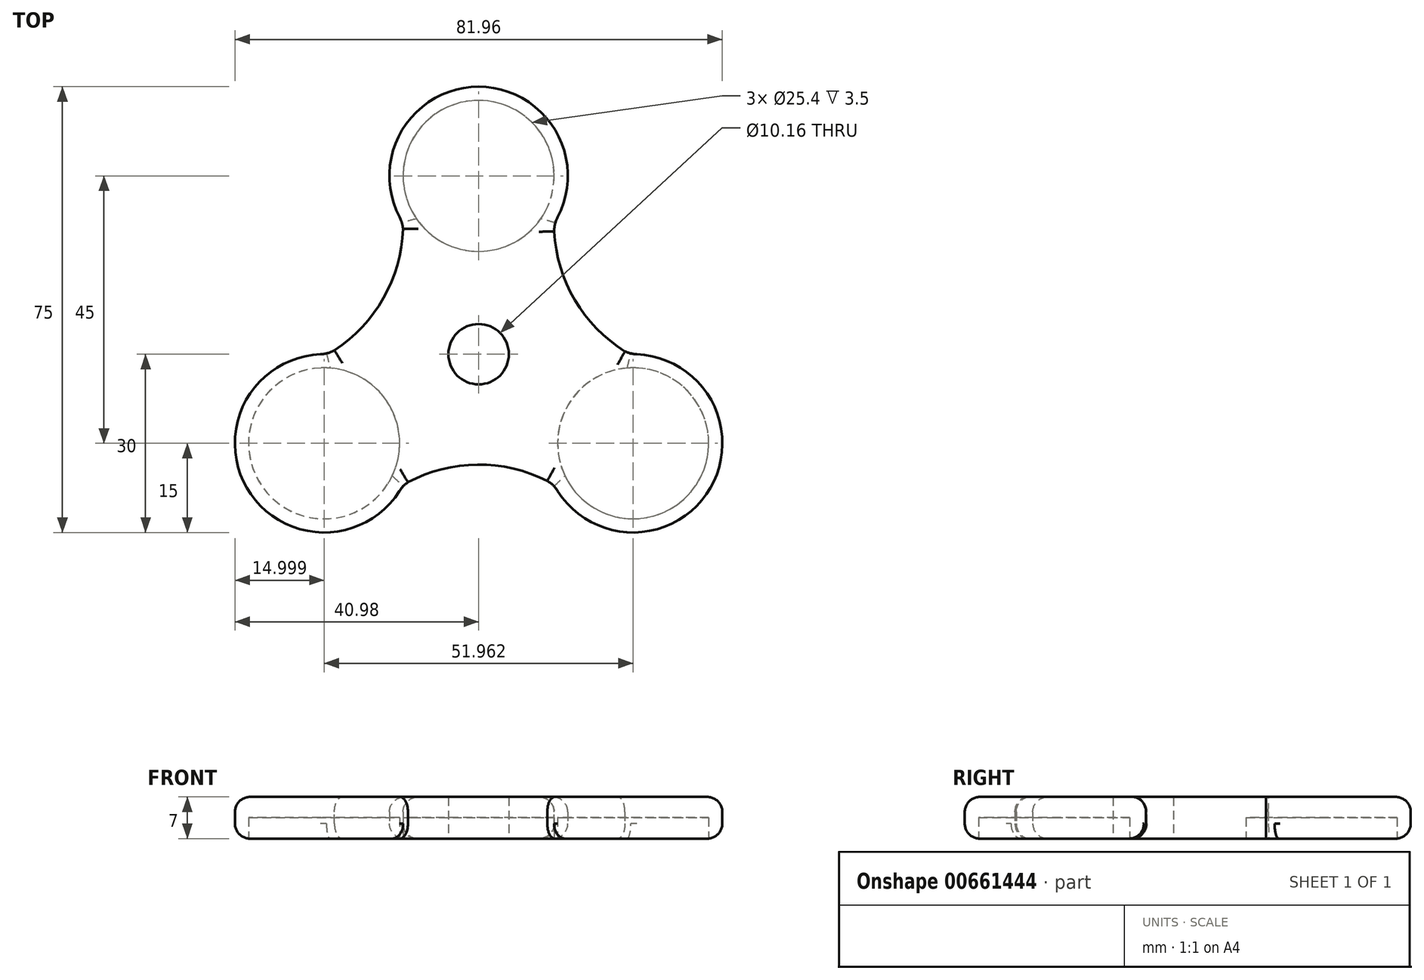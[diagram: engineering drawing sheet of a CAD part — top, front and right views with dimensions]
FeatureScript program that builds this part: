
annotation { "Feature Type Name" : "Feature", "Feature Type Description" : "" }
export const myFeature = defineFeature(function(context is Context, id is Id, definition is map)
    precondition{}
    {
        {
            var Q0;
            Q0=qCreatedBy(makeId("Top.planeOp"),FACE);
            var sketch = newSketch(context, id + "F0", { "sketchPlane" : qUnion([Q0])});
            skCircle(sketch, "E0", {"center": v(0, 0) * mm, "radius": 15 * mm});
            skCircle(sketch, "E1", {"center": v(0, 30) * mm, "radius": 15 * mm});
            skCircle(sketch, "E2", {"center": v(0, 30) * mm, "radius": 12.7 * mm});
            skCircle(sketch, "E3", {"center": v(0, 0) * mm, "radius": 5.08 * mm});
            skLineSegment(sketch, "E4", {"start": v(0, 30) * mm, "end": v(0, 15) * mm, "construction": true});
            skLineSegment(sketch, "E5", {"start": v(0, 0) * mm, "end": v(0, 15) * mm, "construction": true});
            skLineSegment(sketch, "E6", {"start": v(0, 0) * mm, "end": v(0, -15) * mm});
            skLineSegment(sketch, "E7", {"start": v(0, 0) * mm, "end": v(15, 0) * mm});
            skLineSegment(sketch, "E8", {"start": v(0, 0) * mm, "end": v(-15, 0) * mm});
            skLineSegment(sketch, "E9", {"start": v(0, 30) * mm, "end": v(-20.54, 30) * mm, "construction": true});
            skLineSegment(sketch, "E10", {"start": v(-25.98, -15) * mm, "end": v(-25.98, 30.15) * mm, "construction": true});
            skPoint(sketch, "E11", {"position": v(-25.98, 0) * mm});
            skPoint(sketch, "E12", {"position": v(-15, 30) * mm});
            skLineSegment(sketch, "E13.0", {"start": v(12.7, 30) * mm, "end": v(12.7, 15) * mm});
            skLineSegment(sketch, "E13.1", {"start": v(12.7, 0) * mm, "end": v(12.7, 15) * mm});
            skLineSegment(sketch, "E14.0", {"start": v(-12.7, 30) * mm, "end": v(-12.7, 15) * mm});
            skLineSegment(sketch, "E14.1", {"start": v(-12.7, 0) * mm, "end": v(-12.7, 15) * mm});
            skPoint(sketch, "E15.1.0", {"position": v(-18.48, -28) * mm});
            skLineSegment(sketch, "E15.1.1", {"start": v(-19.63, -26) * mm, "end": v(-6.64, -18.5) * mm});
            skLineSegment(sketch, "E15.1.2", {"start": v(-32.33, -4) * mm, "end": v(-19.34, 3.5) * mm});
            skLineSegment(sketch, "E15.1.3", {"start": v(-25.98, -15) * mm, "end": v(-15.71, -32.78) * mm, "construction": true});
            skLineSegment(sketch, "E15.1.4", {"start": v(-25.98, -15) * mm, "end": v(-13, -7.5) * mm, "construction": true});
            skCircle(sketch, "E15.1.5", {"center": v(-25.98, -15) * mm, "radius": 12.7 * mm});
            skCircle(sketch, "E15.1.6", {"center": v(-25.98, -15) * mm, "radius": 15 * mm});
            skLineSegment(sketch, "E15.1.7", {"start": v(6.35, -11) * mm, "end": v(-6.64, -18.5) * mm});
            skLineSegment(sketch, "E15.1.8", {"start": v(-6.35, 11) * mm, "end": v(-19.34, 3.5) * mm});
            skLineSegment(sketch, "E15.1.9", {"start": v(0, 0) * mm, "end": v(-13, -7.5) * mm, "construction": true});
            skPoint(sketch, "E15.2.0", {"position": v(33.48, -2) * mm});
            skLineSegment(sketch, "E15.2.1", {"start": v(32.33, -4) * mm, "end": v(19.34, 3.5) * mm});
            skLineSegment(sketch, "E15.2.2", {"start": v(19.63, -26) * mm, "end": v(6.64, -18.5) * mm});
            skLineSegment(sketch, "E15.2.3", {"start": v(25.98, -15) * mm, "end": v(36.25, 2.78) * mm, "construction": true});
            skLineSegment(sketch, "E15.2.4", {"start": v(25.98, -15) * mm, "end": v(13, -7.5) * mm, "construction": true});
            skCircle(sketch, "E15.2.5", {"center": v(25.98, -15) * mm, "radius": 12.7 * mm});
            skCircle(sketch, "E15.2.6", {"center": v(25.98, -15) * mm, "radius": 15 * mm});
            skLineSegment(sketch, "E15.2.7", {"start": v(6.35, 11) * mm, "end": v(19.34, 3.5) * mm});
            skLineSegment(sketch, "E15.2.8", {"start": v(-6.35, -11) * mm, "end": v(6.64, -18.5) * mm});
            skLineSegment(sketch, "E15.2.9", {"start": v(0, 0) * mm, "end": v(13, -7.5) * mm, "construction": true});
            skSolve(sketch);
        }
        {
            var Q0;
            {var subQ0=sQuery(id+"F0.wireOp",EDGE,"E14.0");var subQ1=sQuery(id+"F0.wireOp",EDGE,"E1");var subQ2=makeQuery(id+"F0.imprint","INTERSECT",VERTEX,{"derivedFrom":[subQ1,subQ0]});Q0=makeQuery(id+"F0.imprint","IMPRINT",FACE,{"disambiguationData":[TD([[makeQuery(id+"F0.imprint","IMPRINT",EDGE,{"disambiguationData":[TD([[subQ2,1.0]])],"derivedFrom":subQ1}),1.0]])]});}
            var Q1;
            {var subQ0=sQuery(id+"F0.wireOp",EDGE,"E13.1");var subQ1=sQuery(id+"F0.wireOp",EDGE,"E0");var subQ2=makeQuery(id+"F0.imprint","INTERSECT",VERTEX,{"derivedFrom":[subQ1,subQ0]});Q1=makeQuery(id+"F0.imprint","IMPRINT",FACE,{"disambiguationData":[TD([[makeQuery(id+"F0.imprint","IMPRINT",EDGE,{"disambiguationData":[TD([[subQ2,-1.0]])],"derivedFrom":subQ1}),-1.0]])]});}
            var Q2;
            {var subQ0=sQuery(id+"F0.wireOp",EDGE,"E14.1");var subQ1=sQuery(id+"F0.wireOp",EDGE,"E0");var subQ2=makeQuery(id+"F0.imprint","INTERSECT",VERTEX,{"derivedFrom":[subQ1,subQ0]});Q2=makeQuery(id+"F0.imprint","IMPRINT",FACE,{"disambiguationData":[TD([[makeQuery(id+"F0.imprint","IMPRINT",EDGE,{"disambiguationData":[TD([[subQ2,1.0]])],"derivedFrom":subQ1}),-1.0]])]});}
            var Q3;
            {var subQ1=sQuery(id+"F0.wireOp",EDGE,"E1");var subQ5=sQuery(id+"F0.wireOp",EDGE,"E14.0");var subQ8=makeQuery(id+"F0.imprint","INTERSECT",VERTEX,{"derivedFrom":[subQ1,subQ5]});Q3=makeQuery(id+"F0.imprint","IMPRINT",FACE,{"disambiguationData":[TD([[makeQuery(id+"F0.imprint","IMPRINT",EDGE,{"disambiguationData":[TD([[subQ8,-1.0]])],"derivedFrom":subQ1}),1.0]])]});}
            var Q4;
            {var subQ0=sQuery(id+"F0.wireOp",EDGE,"E13.1");var subQ5=sQuery(id+"F0.wireOp",EDGE,"E0");var subQ6=makeQuery(id+"F0.imprint","INTERSECT",VERTEX,{"derivedFrom":[subQ5,subQ0]});Q4=makeQuery(id+"F0.imprint","IMPRINT",FACE,{"disambiguationData":[TD([[makeQuery(id+"F0.imprint","IMPRINT",EDGE,{"disambiguationData":[TD([[subQ6,-1.0]])],"derivedFrom":subQ5}),1.0]])]});}
            var Q5;
            {var subQ0=sQuery(id+"F0.wireOp",EDGE,"E7");var subQ1=sQuery(id+"F0.wireOp",EDGE,"E0");var subQ2=makeQuery(id+"F0.imprint","INTERSECT",VERTEX,{"derivedFrom":[subQ1,subQ0]});Q5=makeQuery(id+"F0.imprint","IMPRINT",FACE,{"disambiguationData":[TD([[makeQuery(id+"F0.imprint","IMPRINT",EDGE,{"disambiguationData":[TD([[subQ2,-1.0]])],"derivedFrom":subQ1}),1.0]])]});}
            var Q6;
            {var subQ3=sQuery(id+"F0.wireOp",EDGE,"E0");var subQ7=makeQuery(id+"F0.imprint","INTERSECT",VERTEX,{"derivedFrom":[subQ3,sQuery(id+"F0.wireOp",EDGE,"E7")]});Q6=makeQuery(id+"F0.imprint","IMPRINT",FACE,{"disambiguationData":[TD([[makeQuery(id+"F0.imprint","IMPRINT",EDGE,{"disambiguationData":[TD([[subQ7,-1.0]])],"derivedFrom":subQ3}),-1.0]])]});}
            var Q7;
            {var subQ0=sQuery(id+"F0.wireOp",EDGE,"E15.2.6");var subQ1=sQuery(id+"F0.wireOp",EDGE,"E15.2.1");var subQ2=makeQuery(id+"F0.imprint","INTERSECT",VERTEX,{"derivedFrom":[subQ1,subQ0]});Q7=makeQuery(id+"F0.imprint","IMPRINT",FACE,{"disambiguationData":[TD([[makeQuery(id+"F0.imprint","IMPRINT",EDGE,{"disambiguationData":[TD([[subQ2,1.0]])],"derivedFrom":subQ1}),1.0]])]});}
            var Q8;
            {var subQ0=sQuery(id+"F0.wireOp",EDGE,"E15.2.6");var subQ1=sQuery(id+"F0.wireOp",EDGE,"E15.2.1");var subQ2=makeQuery(id+"F0.imprint","INTERSECT",VERTEX,{"derivedFrom":[subQ1,subQ0]});Q8=makeQuery(id+"F0.imprint","IMPRINT",FACE,{"disambiguationData":[TD([[makeQuery(id+"F0.imprint","IMPRINT",EDGE,{"disambiguationData":[TD([[subQ2,1.0]])],"derivedFrom":subQ1}),-1.0]])]});}
            var Q9;
            {var subQ0=sQuery(id+"F0.wireOp",EDGE,"E15.2.8");var subQ1=sQuery(id+"F0.wireOp",EDGE,"E0");var subQ2=makeQuery(id+"F0.imprint","INTERSECT",VERTEX,{"derivedFrom":[subQ1,subQ0]});Q9=makeQuery(id+"F0.imprint","IMPRINT",FACE,{"disambiguationData":[TD([[makeQuery(id+"F0.imprint","IMPRINT",EDGE,{"disambiguationData":[TD([[subQ2,-1.0]])],"derivedFrom":subQ1}),-1.0]])]});}
            var Q10;
            {var subQ5=sQuery(id+"F0.wireOp",EDGE,"E15.2.8");var subQ6=sQuery(id+"F0.wireOp",EDGE,"E0");var subQ7=makeQuery(id+"F0.imprint","INTERSECT",VERTEX,{"derivedFrom":[subQ6,subQ5]});Q10=makeQuery(id+"F0.imprint","IMPRINT",FACE,{"disambiguationData":[TD([[makeQuery(id+"F0.imprint","IMPRINT",EDGE,{"disambiguationData":[TD([[subQ7,-1.0]])],"derivedFrom":subQ6}),1.0]])]});}
            var Q11;
            {var subQ0=sQuery(id+"F0.wireOp",EDGE,"E8");var subQ6=sQuery(id+"F0.wireOp",EDGE,"E0");var subQ10=makeQuery(id+"F0.imprint","INTERSECT",VERTEX,{"derivedFrom":[subQ6,subQ0]});Q11=makeQuery(id+"F0.imprint","IMPRINT",FACE,{"disambiguationData":[TD([[makeQuery(id+"F0.imprint","IMPRINT",EDGE,{"disambiguationData":[TD([[subQ10,-1.0]])],"derivedFrom":subQ6}),1.0]])]});}
            var Q12;
            {var subQ0=sQuery(id+"F0.wireOp",EDGE,"E8");var subQ1=sQuery(id+"F0.wireOp",EDGE,"E0");var subQ2=makeQuery(id+"F0.imprint","INTERSECT",VERTEX,{"derivedFrom":[subQ1,subQ0]});Q12=makeQuery(id+"F0.imprint","IMPRINT",FACE,{"disambiguationData":[TD([[makeQuery(id+"F0.imprint","IMPRINT",EDGE,{"disambiguationData":[TD([[subQ2,1.0]])],"derivedFrom":subQ1}),1.0]])]});}
            var Q13;
            {var subQ5=sQuery(id+"F0.wireOp",EDGE,"E0");var subQ7=makeQuery(id+"F0.imprint","INTERSECT",VERTEX,{"derivedFrom":[subQ5,sQuery(id+"F0.wireOp",EDGE,"E8")]});Q13=makeQuery(id+"F0.imprint","IMPRINT",FACE,{"disambiguationData":[TD([[makeQuery(id+"F0.imprint","IMPRINT",EDGE,{"disambiguationData":[TD([[subQ7,1.0]])],"derivedFrom":subQ5}),-1.0]])]});}
            var Q14;
            {var subQ0=sQuery(id+"F0.wireOp",EDGE,"E15.1.6");var subQ1=sQuery(id+"F0.wireOp",EDGE,"E15.1.1");var subQ2=makeQuery(id+"F0.imprint","INTERSECT",VERTEX,{"derivedFrom":[subQ1,subQ0]});Q14=makeQuery(id+"F0.imprint","IMPRINT",FACE,{"disambiguationData":[TD([[makeQuery(id+"F0.imprint","IMPRINT",EDGE,{"disambiguationData":[TD([[subQ2,1.0]])],"derivedFrom":subQ1}),1.0]])]});}
            var Q15;
            {var subQ0=sQuery(id+"F0.wireOp",EDGE,"E15.1.6");var subQ1=sQuery(id+"F0.wireOp",EDGE,"E15.1.1");var subQ2=makeQuery(id+"F0.imprint","INTERSECT",VERTEX,{"derivedFrom":[subQ1,subQ0]});Q15=makeQuery(id+"F0.imprint","IMPRINT",FACE,{"disambiguationData":[TD([[makeQuery(id+"F0.imprint","IMPRINT",EDGE,{"disambiguationData":[TD([[subQ2,1.0]])],"derivedFrom":subQ1}),-1.0]])]});}
            var Q16;
            Q16=makeQuery(id+"F0.imprint","IMPRINT",FACE,{"disambiguationData":[TD([[makeQuery(id+"F0.imprint","IMPRINT",EDGE,{"derivedFrom":sQuery(id+"F0.wireOp",EDGE,"E15.1.5")}),-1.0]])]});
            var Q17;
            Q17=makeQuery(id+"F0.imprint","IMPRINT",FACE,{"disambiguationData":[TD([[makeQuery(id+"F0.imprint","IMPRINT",EDGE,{"derivedFrom":sQuery(id+"F0.wireOp",EDGE,"E15.2.5")}),-1.0]])]});
            var Q18;
            {var subQ0=sQuery(id+"F0.wireOp",EDGE,"E15.1.7");var subQ1=sQuery(id+"F0.wireOp",EDGE,"E0");var subQ2=makeQuery(id+"F0.imprint","INTERSECT",VERTEX,{"derivedFrom":[subQ1,subQ0]});Q18=makeQuery(id+"F0.imprint","IMPRINT",FACE,{"disambiguationData":[TD([[makeQuery(id+"F0.imprint","IMPRINT",EDGE,{"disambiguationData":[TD([[subQ2,1.0]])],"derivedFrom":subQ1}),-1.0]])]});}
            extrude(context, id + "F1", {"entities" : qUnion([Q0, Q1, Q2, Q3, Q4, Q5, Q6, Q7, Q8, Q9, Q10, Q11, Q12, Q13, Q14, Q15, Q16, Q17, Q18]), "endBound" : BoundingType.SYMMETRIC, "depth" : 7 * mm, "offsetDistance" : 25.4 * mm});
        }
        {
            var Q0;
            Q0=makeQuery(id+"F1.opExtrude","SWEPT_EDGE",EDGE,{"disambiguationData":[OSD([sQuery(id+"F0.wireOp",EDGE,"E1"),sQuery(id+"F0.wireOp",EDGE,"E14.0")])]});
            var Q1;
            Q1=makeQuery(id+"F1.opExtrude","SWEPT_EDGE",EDGE,{"disambiguationData":[OSD([sQuery(id+"F0.wireOp",EDGE,"E15.1.2"),sQuery(id+"F0.wireOp",EDGE,"E15.1.6")])]});
            var Q2;
            Q2=makeQuery(id+"F1.opExtrude","SWEPT_EDGE",EDGE,{"disambiguationData":[OSD([sQuery(id+"F0.wireOp",EDGE,"E15.1.1"),sQuery(id+"F0.wireOp",EDGE,"E15.1.6")])]});
            var Q3;
            Q3=makeQuery(id+"F1.opExtrude","SWEPT_EDGE",EDGE,{"disambiguationData":[OSD([sQuery(id+"F0.wireOp",EDGE,"E15.2.2"),sQuery(id+"F0.wireOp",EDGE,"E15.2.6")])]});
            var Q4;
            Q4=makeQuery(id+"F1.opExtrude","SWEPT_EDGE",EDGE,{"disambiguationData":[OSD([sQuery(id+"F0.wireOp",EDGE,"E15.2.1"),sQuery(id+"F0.wireOp",EDGE,"E15.2.6")])]});
            var Q5;
            Q5=makeQuery(id+"F1.opExtrude","SWEPT_EDGE",EDGE,{"disambiguationData":[OSD([sQuery(id+"F0.wireOp",EDGE,"E1"),sQuery(id+"F0.wireOp",EDGE,"E13.0")])]});
            fillet(context, id + "F2", {"entities" : qUnion([Q0, Q1, Q2, Q3, Q4, Q5]), "radius" : 5.08 * mm, "tangentPropagation" : true, "allowEdgeOverflow" : false});
        }
        {
            var Q0;
            Q0=makeQuery(id+"F1.opExtrude","SWEPT_EDGE",EDGE,{"disambiguationData":[OSD([sQuery(id+"F0.wireOp",EDGE,"E13.1"),sQuery(id+"F0.wireOp",EDGE,"E15.2.7")])]});
            var Q1;
            Q1=makeQuery(id+"F1.opExtrude","SWEPT_EDGE",EDGE,{"disambiguationData":[OSD([sQuery(id+"F0.wireOp",EDGE,"E14.1"),sQuery(id+"F0.wireOp",EDGE,"E15.1.8")])]});
            var Q2;
            Q2=makeQuery(id+"F1.opExtrude","SWEPT_EDGE",EDGE,{"disambiguationData":[OSD([sQuery(id+"F0.wireOp",EDGE,"E6"),sQuery(id+"F0.wireOp",EDGE,"E15.1.7"),sQuery(id+"F0.wireOp",EDGE,"E15.2.8")])]});
            fillet(context, id + "F3", {"entities" : qUnion([Q0, Q1, Q2]), "radius" : 25.4 * mm, "tangentPropagation" : true, "allowEdgeOverflow" : false});
        }
        {
            var Q0;
            {var subQ0=sQuery(id+"F0.wireOp",EDGE,"E2");var subQ1=makeQuery(id+"F0.imprint","INTERSECT",VERTEX,{"derivedFrom":[subQ0,sQuery(id+"F0.wireOp",EDGE,"E13.0")]});Q0=makeQuery(id+"F0.imprint","IMPRINT",FACE,{"disambiguationData":[TD([[makeQuery(id+"F0.imprint","IMPRINT",EDGE,{"disambiguationData":[TD([[subQ1,1.0]])],"derivedFrom":subQ0}),1.0]])]});}
            var Q1;
            {var subQ0=sQuery(id+"F0.wireOp",EDGE,"E15.2.5");var subQ1=makeQuery(id+"F0.imprint","INTERSECT",VERTEX,{"derivedFrom":[sQuery(id+"F0.wireOp",EDGE,"E15.2.1"),subQ0]});Q1=makeQuery(id+"F0.imprint","IMPRINT",FACE,{"disambiguationData":[TD([[makeQuery(id+"F0.imprint","IMPRINT",EDGE,{"disambiguationData":[TD([[subQ1,-1.0]])],"derivedFrom":subQ0}),1.0]])]});}
            var Q2;
            {var subQ0=sQuery(id+"F0.wireOp",EDGE,"E15.1.5");var subQ1=makeQuery(id+"F0.imprint","INTERSECT",VERTEX,{"derivedFrom":[sQuery(id+"F0.wireOp",EDGE,"E15.1.1"),subQ0]});Q2=makeQuery(id+"F0.imprint","IMPRINT",FACE,{"disambiguationData":[TD([[makeQuery(id+"F0.imprint","IMPRINT",EDGE,{"disambiguationData":[TD([[subQ1,-1.0]])],"derivedFrom":subQ0}),1.0]])]});}
            var Q3;
            Q3=makeQuery(id+"F1.opExtrude","CAP_FACE",FACE,{"disambiguationData":[OSD([sQuery(id+"F0.wireOp",EDGE,"E1"),sQuery(id+"F0.wireOp",EDGE,"E2"),sQuery(id+"F0.wireOp",EDGE,"E3"),sQuery(id+"F0.wireOp",EDGE,"E13.0"),sQuery(id+"F0.wireOp",EDGE,"E13.1"),sQuery(id+"F0.wireOp",EDGE,"E14.0"),sQuery(id+"F0.wireOp",EDGE,"E14.1"),sQuery(id+"F0.wireOp",EDGE,"E15.1.1"),sQuery(id+"F0.wireOp",EDGE,"E15.1.2"),sQuery(id+"F0.wireOp",EDGE,"E15.1.5"),sQuery(id+"F0.wireOp",EDGE,"E15.1.6"),sQuery(id+"F0.wireOp",EDGE,"E15.1.7"),sQuery(id+"F0.wireOp",EDGE,"E15.1.8"),sQuery(id+"F0.wireOp",EDGE,"E15.2.1"),sQuery(id+"F0.wireOp",EDGE,"E15.2.2"),sQuery(id+"F0.wireOp",EDGE,"E15.2.5"),sQuery(id+"F0.wireOp",EDGE,"E15.2.6"),sQuery(id+"F0.wireOp",EDGE,"E15.2.7"),sQuery(id+"F0.wireOp",EDGE,"E15.2.8")])],"isStart":false});
            extrude(context, id + "F4", {"entities" : qUnion([Q0, Q1, Q2]), "operationType" : NewBodyOperationType.ADD, "endBound" : BoundingType.UP_TO_SURFACE, "depth" : 25.4 * mm, "endBoundEntityFace" : qUnion([Q3]), "offsetDistance" : 25.4 * mm});
        }
        {
            var Q0;
            {var subQ0=sQuery(id+"F0.wireOp",EDGE,"E15.2.8");var subQ1=sQuery(id+"F0.wireOp",EDGE,"E15.1.7");Q0=makeQuery(id+"F3.opFillet","BLEND_EDGE",EDGE,{"blendedFrom":[makeQuery(id+"F1.opExtrude","SWEPT_EDGE",EDGE,{"disambiguationData":[OSD([sQuery(id+"F0.wireOp",EDGE,"E6"),subQ1,subQ0])]}),makeQuery(id+"F1.opExtrude","CAP_FACE",FACE,{"disambiguationData":[OSD([sQuery(id+"F0.wireOp",EDGE,"E1"),sQuery(id+"F0.wireOp",EDGE,"E2"),sQuery(id+"F0.wireOp",EDGE,"E3"),sQuery(id+"F0.wireOp",EDGE,"E13.0"),sQuery(id+"F0.wireOp",EDGE,"E13.1"),sQuery(id+"F0.wireOp",EDGE,"E14.0"),sQuery(id+"F0.wireOp",EDGE,"E14.1"),sQuery(id+"F0.wireOp",EDGE,"E15.1.1"),sQuery(id+"F0.wireOp",EDGE,"E15.1.2"),sQuery(id+"F0.wireOp",EDGE,"E15.1.5"),sQuery(id+"F0.wireOp",EDGE,"E15.1.6"),subQ1,sQuery(id+"F0.wireOp",EDGE,"E15.1.8"),sQuery(id+"F0.wireOp",EDGE,"E15.2.1"),sQuery(id+"F0.wireOp",EDGE,"E15.2.2"),sQuery(id+"F0.wireOp",EDGE,"E15.2.5"),sQuery(id+"F0.wireOp",EDGE,"E15.2.6"),sQuery(id+"F0.wireOp",EDGE,"E15.2.7"),subQ0])],"isStart":false})],"blendedInto":[makeQuery(id+"F1.opExtrude","CAP_FACE",FACE,{"disambiguationData":[OSD([sQuery(id+"F0.wireOp",EDGE,"E1"),sQuery(id+"F0.wireOp",EDGE,"E2"),sQuery(id+"F0.wireOp",EDGE,"E3"),sQuery(id+"F0.wireOp",EDGE,"E13.0"),sQuery(id+"F0.wireOp",EDGE,"E13.1"),sQuery(id+"F0.wireOp",EDGE,"E14.0"),sQuery(id+"F0.wireOp",EDGE,"E14.1"),sQuery(id+"F0.wireOp",EDGE,"E15.1.1"),sQuery(id+"F0.wireOp",EDGE,"E15.1.2"),sQuery(id+"F0.wireOp",EDGE,"E15.1.5"),sQuery(id+"F0.wireOp",EDGE,"E15.1.6"),subQ1,sQuery(id+"F0.wireOp",EDGE,"E15.1.8"),sQuery(id+"F0.wireOp",EDGE,"E15.2.1"),sQuery(id+"F0.wireOp",EDGE,"E15.2.2"),sQuery(id+"F0.wireOp",EDGE,"E15.2.5"),sQuery(id+"F0.wireOp",EDGE,"E15.2.6"),sQuery(id+"F0.wireOp",EDGE,"E15.2.7"),subQ0])],"isStart":false})]});}
            var Q1;
            {var subQ0=sQuery(id+"F0.wireOp",EDGE,"E15.1.6");var subQ1=sQuery(id+"F0.wireOp",EDGE,"E15.1.1");Q1=makeQuery(id+"F2.opFillet","BLEND_EDGE",EDGE,{"blendedFrom":[makeQuery(id+"F1.opExtrude","SWEPT_EDGE",EDGE,{"disambiguationData":[OSD([subQ1,subQ0])]}),makeQuery(id+"F1.opExtrude","CAP_FACE",FACE,{"disambiguationData":[OSD([sQuery(id+"F0.wireOp",EDGE,"E1"),sQuery(id+"F0.wireOp",EDGE,"E2"),sQuery(id+"F0.wireOp",EDGE,"E3"),sQuery(id+"F0.wireOp",EDGE,"E13.0"),sQuery(id+"F0.wireOp",EDGE,"E13.1"),sQuery(id+"F0.wireOp",EDGE,"E14.0"),sQuery(id+"F0.wireOp",EDGE,"E14.1"),subQ1,sQuery(id+"F0.wireOp",EDGE,"E15.1.2"),sQuery(id+"F0.wireOp",EDGE,"E15.1.5"),subQ0,sQuery(id+"F0.wireOp",EDGE,"E15.1.7"),sQuery(id+"F0.wireOp",EDGE,"E15.1.8"),sQuery(id+"F0.wireOp",EDGE,"E15.2.1"),sQuery(id+"F0.wireOp",EDGE,"E15.2.2"),sQuery(id+"F0.wireOp",EDGE,"E15.2.5"),sQuery(id+"F0.wireOp",EDGE,"E15.2.6"),sQuery(id+"F0.wireOp",EDGE,"E15.2.7"),sQuery(id+"F0.wireOp",EDGE,"E15.2.8")])],"isStart":false})],"blendedInto":[makeQuery(id+"F1.opExtrude","CAP_FACE",FACE,{"disambiguationData":[OSD([sQuery(id+"F0.wireOp",EDGE,"E1"),sQuery(id+"F0.wireOp",EDGE,"E2"),sQuery(id+"F0.wireOp",EDGE,"E3"),sQuery(id+"F0.wireOp",EDGE,"E13.0"),sQuery(id+"F0.wireOp",EDGE,"E13.1"),sQuery(id+"F0.wireOp",EDGE,"E14.0"),sQuery(id+"F0.wireOp",EDGE,"E14.1"),subQ1,sQuery(id+"F0.wireOp",EDGE,"E15.1.2"),sQuery(id+"F0.wireOp",EDGE,"E15.1.5"),subQ0,sQuery(id+"F0.wireOp",EDGE,"E15.1.7"),sQuery(id+"F0.wireOp",EDGE,"E15.1.8"),sQuery(id+"F0.wireOp",EDGE,"E15.2.1"),sQuery(id+"F0.wireOp",EDGE,"E15.2.2"),sQuery(id+"F0.wireOp",EDGE,"E15.2.5"),sQuery(id+"F0.wireOp",EDGE,"E15.2.6"),sQuery(id+"F0.wireOp",EDGE,"E15.2.7"),sQuery(id+"F0.wireOp",EDGE,"E15.2.8")])],"isStart":false})]});}
            var Q2;
            Q2=makeQuery(id+"F1.opExtrude","CAP_EDGE",EDGE,{"disambiguationData":[OSD([sQuery(id+"F0.wireOp",EDGE,"E15.1.6")])],"isStart":false});
            var Q3;
            {var subQ0=sQuery(id+"F0.wireOp",EDGE,"E15.2.6");var subQ1=sQuery(id+"F0.wireOp",EDGE,"E15.2.2");Q3=makeQuery(id+"F2.opFillet","BLEND_EDGE",EDGE,{"blendedFrom":[makeQuery(id+"F1.opExtrude","SWEPT_EDGE",EDGE,{"disambiguationData":[OSD([subQ1,subQ0])]}),makeQuery(id+"F1.opExtrude","CAP_FACE",FACE,{"disambiguationData":[OSD([sQuery(id+"F0.wireOp",EDGE,"E1"),sQuery(id+"F0.wireOp",EDGE,"E2"),sQuery(id+"F0.wireOp",EDGE,"E3"),sQuery(id+"F0.wireOp",EDGE,"E13.0"),sQuery(id+"F0.wireOp",EDGE,"E13.1"),sQuery(id+"F0.wireOp",EDGE,"E14.0"),sQuery(id+"F0.wireOp",EDGE,"E14.1"),sQuery(id+"F0.wireOp",EDGE,"E15.1.1"),sQuery(id+"F0.wireOp",EDGE,"E15.1.2"),sQuery(id+"F0.wireOp",EDGE,"E15.1.5"),sQuery(id+"F0.wireOp",EDGE,"E15.1.6"),sQuery(id+"F0.wireOp",EDGE,"E15.1.7"),sQuery(id+"F0.wireOp",EDGE,"E15.1.8"),sQuery(id+"F0.wireOp",EDGE,"E15.2.1"),subQ1,sQuery(id+"F0.wireOp",EDGE,"E15.2.5"),subQ0,sQuery(id+"F0.wireOp",EDGE,"E15.2.7"),sQuery(id+"F0.wireOp",EDGE,"E15.2.8")])],"isStart":false})],"blendedInto":[makeQuery(id+"F1.opExtrude","CAP_FACE",FACE,{"disambiguationData":[OSD([sQuery(id+"F0.wireOp",EDGE,"E1"),sQuery(id+"F0.wireOp",EDGE,"E2"),sQuery(id+"F0.wireOp",EDGE,"E3"),sQuery(id+"F0.wireOp",EDGE,"E13.0"),sQuery(id+"F0.wireOp",EDGE,"E13.1"),sQuery(id+"F0.wireOp",EDGE,"E14.0"),sQuery(id+"F0.wireOp",EDGE,"E14.1"),sQuery(id+"F0.wireOp",EDGE,"E15.1.1"),sQuery(id+"F0.wireOp",EDGE,"E15.1.2"),sQuery(id+"F0.wireOp",EDGE,"E15.1.5"),sQuery(id+"F0.wireOp",EDGE,"E15.1.6"),sQuery(id+"F0.wireOp",EDGE,"E15.1.7"),sQuery(id+"F0.wireOp",EDGE,"E15.1.8"),sQuery(id+"F0.wireOp",EDGE,"E15.2.1"),subQ1,sQuery(id+"F0.wireOp",EDGE,"E15.2.5"),subQ0,sQuery(id+"F0.wireOp",EDGE,"E15.2.7"),sQuery(id+"F0.wireOp",EDGE,"E15.2.8")])],"isStart":false})]});}
            var Q4;
            Q4=makeQuery(id+"F1.opExtrude","CAP_EDGE",EDGE,{"disambiguationData":[OSD([sQuery(id+"F0.wireOp",EDGE,"E15.2.6")])],"isStart":false});
            var Q5;
            {var subQ0=sQuery(id+"F0.wireOp",EDGE,"E15.2.7");var subQ1=sQuery(id+"F0.wireOp",EDGE,"E13.1");Q5=makeQuery(id+"F3.opFillet","BLEND_EDGE",EDGE,{"blendedFrom":[makeQuery(id+"F1.opExtrude","SWEPT_EDGE",EDGE,{"disambiguationData":[OSD([subQ1,subQ0])]}),makeQuery(id+"F1.opExtrude","CAP_FACE",FACE,{"disambiguationData":[OSD([sQuery(id+"F0.wireOp",EDGE,"E1"),sQuery(id+"F0.wireOp",EDGE,"E2"),sQuery(id+"F0.wireOp",EDGE,"E3"),sQuery(id+"F0.wireOp",EDGE,"E13.0"),subQ1,sQuery(id+"F0.wireOp",EDGE,"E14.0"),sQuery(id+"F0.wireOp",EDGE,"E14.1"),sQuery(id+"F0.wireOp",EDGE,"E15.1.1"),sQuery(id+"F0.wireOp",EDGE,"E15.1.2"),sQuery(id+"F0.wireOp",EDGE,"E15.1.5"),sQuery(id+"F0.wireOp",EDGE,"E15.1.6"),sQuery(id+"F0.wireOp",EDGE,"E15.1.7"),sQuery(id+"F0.wireOp",EDGE,"E15.1.8"),sQuery(id+"F0.wireOp",EDGE,"E15.2.1"),sQuery(id+"F0.wireOp",EDGE,"E15.2.2"),sQuery(id+"F0.wireOp",EDGE,"E15.2.5"),sQuery(id+"F0.wireOp",EDGE,"E15.2.6"),subQ0,sQuery(id+"F0.wireOp",EDGE,"E15.2.8")])],"isStart":false})],"blendedInto":[makeQuery(id+"F1.opExtrude","CAP_FACE",FACE,{"disambiguationData":[OSD([sQuery(id+"F0.wireOp",EDGE,"E1"),sQuery(id+"F0.wireOp",EDGE,"E2"),sQuery(id+"F0.wireOp",EDGE,"E3"),sQuery(id+"F0.wireOp",EDGE,"E13.0"),subQ1,sQuery(id+"F0.wireOp",EDGE,"E14.0"),sQuery(id+"F0.wireOp",EDGE,"E14.1"),sQuery(id+"F0.wireOp",EDGE,"E15.1.1"),sQuery(id+"F0.wireOp",EDGE,"E15.1.2"),sQuery(id+"F0.wireOp",EDGE,"E15.1.5"),sQuery(id+"F0.wireOp",EDGE,"E15.1.6"),sQuery(id+"F0.wireOp",EDGE,"E15.1.7"),sQuery(id+"F0.wireOp",EDGE,"E15.1.8"),sQuery(id+"F0.wireOp",EDGE,"E15.2.1"),sQuery(id+"F0.wireOp",EDGE,"E15.2.2"),sQuery(id+"F0.wireOp",EDGE,"E15.2.5"),sQuery(id+"F0.wireOp",EDGE,"E15.2.6"),subQ0,sQuery(id+"F0.wireOp",EDGE,"E15.2.8")])],"isStart":false})]});}
            var Q6;
            {var subQ0=sQuery(id+"F0.wireOp",EDGE,"E15.2.6");var subQ1=sQuery(id+"F0.wireOp",EDGE,"E15.2.1");Q6=makeQuery(id+"F2.opFillet","BLEND_EDGE",EDGE,{"blendedFrom":[makeQuery(id+"F1.opExtrude","SWEPT_EDGE",EDGE,{"disambiguationData":[OSD([subQ1,subQ0])]}),makeQuery(id+"F1.opExtrude","CAP_FACE",FACE,{"disambiguationData":[OSD([sQuery(id+"F0.wireOp",EDGE,"E1"),sQuery(id+"F0.wireOp",EDGE,"E2"),sQuery(id+"F0.wireOp",EDGE,"E3"),sQuery(id+"F0.wireOp",EDGE,"E13.0"),sQuery(id+"F0.wireOp",EDGE,"E13.1"),sQuery(id+"F0.wireOp",EDGE,"E14.0"),sQuery(id+"F0.wireOp",EDGE,"E14.1"),sQuery(id+"F0.wireOp",EDGE,"E15.1.1"),sQuery(id+"F0.wireOp",EDGE,"E15.1.2"),sQuery(id+"F0.wireOp",EDGE,"E15.1.5"),sQuery(id+"F0.wireOp",EDGE,"E15.1.6"),sQuery(id+"F0.wireOp",EDGE,"E15.1.7"),sQuery(id+"F0.wireOp",EDGE,"E15.1.8"),subQ1,sQuery(id+"F0.wireOp",EDGE,"E15.2.2"),sQuery(id+"F0.wireOp",EDGE,"E15.2.5"),subQ0,sQuery(id+"F0.wireOp",EDGE,"E15.2.7"),sQuery(id+"F0.wireOp",EDGE,"E15.2.8")])],"isStart":false})],"blendedInto":[makeQuery(id+"F1.opExtrude","CAP_FACE",FACE,{"disambiguationData":[OSD([sQuery(id+"F0.wireOp",EDGE,"E1"),sQuery(id+"F0.wireOp",EDGE,"E2"),sQuery(id+"F0.wireOp",EDGE,"E3"),sQuery(id+"F0.wireOp",EDGE,"E13.0"),sQuery(id+"F0.wireOp",EDGE,"E13.1"),sQuery(id+"F0.wireOp",EDGE,"E14.0"),sQuery(id+"F0.wireOp",EDGE,"E14.1"),sQuery(id+"F0.wireOp",EDGE,"E15.1.1"),sQuery(id+"F0.wireOp",EDGE,"E15.1.2"),sQuery(id+"F0.wireOp",EDGE,"E15.1.5"),sQuery(id+"F0.wireOp",EDGE,"E15.1.6"),sQuery(id+"F0.wireOp",EDGE,"E15.1.7"),sQuery(id+"F0.wireOp",EDGE,"E15.1.8"),subQ1,sQuery(id+"F0.wireOp",EDGE,"E15.2.2"),sQuery(id+"F0.wireOp",EDGE,"E15.2.5"),subQ0,sQuery(id+"F0.wireOp",EDGE,"E15.2.7"),sQuery(id+"F0.wireOp",EDGE,"E15.2.8")])],"isStart":false})]});}
            var Q7;
            {var subQ0=sQuery(id+"F0.wireOp",EDGE,"E13.0");var subQ1=sQuery(id+"F0.wireOp",EDGE,"E1");Q7=makeQuery(id+"F2.opFillet","BLEND_EDGE",EDGE,{"blendedFrom":[makeQuery(id+"F1.opExtrude","SWEPT_EDGE",EDGE,{"disambiguationData":[OSD([subQ1,subQ0])]}),makeQuery(id+"F1.opExtrude","CAP_FACE",FACE,{"disambiguationData":[OSD([subQ1,sQuery(id+"F0.wireOp",EDGE,"E2"),sQuery(id+"F0.wireOp",EDGE,"E3"),subQ0,sQuery(id+"F0.wireOp",EDGE,"E13.1"),sQuery(id+"F0.wireOp",EDGE,"E14.0"),sQuery(id+"F0.wireOp",EDGE,"E14.1"),sQuery(id+"F0.wireOp",EDGE,"E15.1.1"),sQuery(id+"F0.wireOp",EDGE,"E15.1.2"),sQuery(id+"F0.wireOp",EDGE,"E15.1.5"),sQuery(id+"F0.wireOp",EDGE,"E15.1.6"),sQuery(id+"F0.wireOp",EDGE,"E15.1.7"),sQuery(id+"F0.wireOp",EDGE,"E15.1.8"),sQuery(id+"F0.wireOp",EDGE,"E15.2.1"),sQuery(id+"F0.wireOp",EDGE,"E15.2.2"),sQuery(id+"F0.wireOp",EDGE,"E15.2.5"),sQuery(id+"F0.wireOp",EDGE,"E15.2.6"),sQuery(id+"F0.wireOp",EDGE,"E15.2.7"),sQuery(id+"F0.wireOp",EDGE,"E15.2.8")])],"isStart":false})],"blendedInto":[makeQuery(id+"F1.opExtrude","CAP_FACE",FACE,{"disambiguationData":[OSD([subQ1,sQuery(id+"F0.wireOp",EDGE,"E2"),sQuery(id+"F0.wireOp",EDGE,"E3"),subQ0,sQuery(id+"F0.wireOp",EDGE,"E13.1"),sQuery(id+"F0.wireOp",EDGE,"E14.0"),sQuery(id+"F0.wireOp",EDGE,"E14.1"),sQuery(id+"F0.wireOp",EDGE,"E15.1.1"),sQuery(id+"F0.wireOp",EDGE,"E15.1.2"),sQuery(id+"F0.wireOp",EDGE,"E15.1.5"),sQuery(id+"F0.wireOp",EDGE,"E15.1.6"),sQuery(id+"F0.wireOp",EDGE,"E15.1.7"),sQuery(id+"F0.wireOp",EDGE,"E15.1.8"),sQuery(id+"F0.wireOp",EDGE,"E15.2.1"),sQuery(id+"F0.wireOp",EDGE,"E15.2.2"),sQuery(id+"F0.wireOp",EDGE,"E15.2.5"),sQuery(id+"F0.wireOp",EDGE,"E15.2.6"),sQuery(id+"F0.wireOp",EDGE,"E15.2.7"),sQuery(id+"F0.wireOp",EDGE,"E15.2.8")])],"isStart":false})]});}
            var Q8;
            Q8=makeQuery(id+"F1.opExtrude","CAP_EDGE",EDGE,{"disambiguationData":[OSD([sQuery(id+"F0.wireOp",EDGE,"E1")])],"isStart":false});
            var Q9;
            {var subQ0=sQuery(id+"F0.wireOp",EDGE,"E15.1.8");var subQ1=sQuery(id+"F0.wireOp",EDGE,"E14.1");Q9=makeQuery(id+"F3.opFillet","BLEND_EDGE",EDGE,{"blendedFrom":[makeQuery(id+"F1.opExtrude","SWEPT_EDGE",EDGE,{"disambiguationData":[OSD([subQ1,subQ0])]}),makeQuery(id+"F1.opExtrude","CAP_FACE",FACE,{"disambiguationData":[OSD([sQuery(id+"F0.wireOp",EDGE,"E1"),sQuery(id+"F0.wireOp",EDGE,"E2"),sQuery(id+"F0.wireOp",EDGE,"E3"),sQuery(id+"F0.wireOp",EDGE,"E13.0"),sQuery(id+"F0.wireOp",EDGE,"E13.1"),sQuery(id+"F0.wireOp",EDGE,"E14.0"),subQ1,sQuery(id+"F0.wireOp",EDGE,"E15.1.1"),sQuery(id+"F0.wireOp",EDGE,"E15.1.2"),sQuery(id+"F0.wireOp",EDGE,"E15.1.5"),sQuery(id+"F0.wireOp",EDGE,"E15.1.6"),sQuery(id+"F0.wireOp",EDGE,"E15.1.7"),subQ0,sQuery(id+"F0.wireOp",EDGE,"E15.2.1"),sQuery(id+"F0.wireOp",EDGE,"E15.2.2"),sQuery(id+"F0.wireOp",EDGE,"E15.2.5"),sQuery(id+"F0.wireOp",EDGE,"E15.2.6"),sQuery(id+"F0.wireOp",EDGE,"E15.2.7"),sQuery(id+"F0.wireOp",EDGE,"E15.2.8")])],"isStart":false})],"blendedInto":[makeQuery(id+"F1.opExtrude","CAP_FACE",FACE,{"disambiguationData":[OSD([sQuery(id+"F0.wireOp",EDGE,"E1"),sQuery(id+"F0.wireOp",EDGE,"E2"),sQuery(id+"F0.wireOp",EDGE,"E3"),sQuery(id+"F0.wireOp",EDGE,"E13.0"),sQuery(id+"F0.wireOp",EDGE,"E13.1"),sQuery(id+"F0.wireOp",EDGE,"E14.0"),subQ1,sQuery(id+"F0.wireOp",EDGE,"E15.1.1"),sQuery(id+"F0.wireOp",EDGE,"E15.1.2"),sQuery(id+"F0.wireOp",EDGE,"E15.1.5"),sQuery(id+"F0.wireOp",EDGE,"E15.1.6"),sQuery(id+"F0.wireOp",EDGE,"E15.1.7"),subQ0,sQuery(id+"F0.wireOp",EDGE,"E15.2.1"),sQuery(id+"F0.wireOp",EDGE,"E15.2.2"),sQuery(id+"F0.wireOp",EDGE,"E15.2.5"),sQuery(id+"F0.wireOp",EDGE,"E15.2.6"),sQuery(id+"F0.wireOp",EDGE,"E15.2.7"),sQuery(id+"F0.wireOp",EDGE,"E15.2.8")])],"isStart":false})]});}
            var Q10;
            {var subQ0=sQuery(id+"F0.wireOp",EDGE,"E14.0");var subQ1=sQuery(id+"F0.wireOp",EDGE,"E1");Q10=makeQuery(id+"F2.opFillet","BLEND_EDGE",EDGE,{"blendedFrom":[makeQuery(id+"F1.opExtrude","SWEPT_EDGE",EDGE,{"disambiguationData":[OSD([subQ1,subQ0])]}),makeQuery(id+"F1.opExtrude","CAP_FACE",FACE,{"disambiguationData":[OSD([subQ1,sQuery(id+"F0.wireOp",EDGE,"E2"),sQuery(id+"F0.wireOp",EDGE,"E3"),sQuery(id+"F0.wireOp",EDGE,"E13.0"),sQuery(id+"F0.wireOp",EDGE,"E13.1"),subQ0,sQuery(id+"F0.wireOp",EDGE,"E14.1"),sQuery(id+"F0.wireOp",EDGE,"E15.1.1"),sQuery(id+"F0.wireOp",EDGE,"E15.1.2"),sQuery(id+"F0.wireOp",EDGE,"E15.1.5"),sQuery(id+"F0.wireOp",EDGE,"E15.1.6"),sQuery(id+"F0.wireOp",EDGE,"E15.1.7"),sQuery(id+"F0.wireOp",EDGE,"E15.1.8"),sQuery(id+"F0.wireOp",EDGE,"E15.2.1"),sQuery(id+"F0.wireOp",EDGE,"E15.2.2"),sQuery(id+"F0.wireOp",EDGE,"E15.2.5"),sQuery(id+"F0.wireOp",EDGE,"E15.2.6"),sQuery(id+"F0.wireOp",EDGE,"E15.2.7"),sQuery(id+"F0.wireOp",EDGE,"E15.2.8")])],"isStart":false})],"blendedInto":[makeQuery(id+"F1.opExtrude","CAP_FACE",FACE,{"disambiguationData":[OSD([subQ1,sQuery(id+"F0.wireOp",EDGE,"E2"),sQuery(id+"F0.wireOp",EDGE,"E3"),sQuery(id+"F0.wireOp",EDGE,"E13.0"),sQuery(id+"F0.wireOp",EDGE,"E13.1"),subQ0,sQuery(id+"F0.wireOp",EDGE,"E14.1"),sQuery(id+"F0.wireOp",EDGE,"E15.1.1"),sQuery(id+"F0.wireOp",EDGE,"E15.1.2"),sQuery(id+"F0.wireOp",EDGE,"E15.1.5"),sQuery(id+"F0.wireOp",EDGE,"E15.1.6"),sQuery(id+"F0.wireOp",EDGE,"E15.1.7"),sQuery(id+"F0.wireOp",EDGE,"E15.1.8"),sQuery(id+"F0.wireOp",EDGE,"E15.2.1"),sQuery(id+"F0.wireOp",EDGE,"E15.2.2"),sQuery(id+"F0.wireOp",EDGE,"E15.2.5"),sQuery(id+"F0.wireOp",EDGE,"E15.2.6"),sQuery(id+"F0.wireOp",EDGE,"E15.2.7"),sQuery(id+"F0.wireOp",EDGE,"E15.2.8")])],"isStart":false})]});}
            var Q11;
            {var subQ0=sQuery(id+"F0.wireOp",EDGE,"E15.1.8");var subQ1=sQuery(id+"F0.wireOp",EDGE,"E14.1");Q11=makeQuery(id+"F3.opFillet","BLEND_EDGE",EDGE,{"blendedFrom":[makeQuery(id+"F1.opExtrude","SWEPT_EDGE",EDGE,{"disambiguationData":[OSD([subQ1,subQ0])]}),makeQuery(id+"F1.opExtrude","CAP_FACE",FACE,{"disambiguationData":[OSD([sQuery(id+"F0.wireOp",EDGE,"E1"),sQuery(id+"F0.wireOp",EDGE,"E2"),sQuery(id+"F0.wireOp",EDGE,"E3"),sQuery(id+"F0.wireOp",EDGE,"E13.0"),sQuery(id+"F0.wireOp",EDGE,"E13.1"),sQuery(id+"F0.wireOp",EDGE,"E14.0"),subQ1,sQuery(id+"F0.wireOp",EDGE,"E15.1.1"),sQuery(id+"F0.wireOp",EDGE,"E15.1.2"),sQuery(id+"F0.wireOp",EDGE,"E15.1.5"),sQuery(id+"F0.wireOp",EDGE,"E15.1.6"),sQuery(id+"F0.wireOp",EDGE,"E15.1.7"),subQ0,sQuery(id+"F0.wireOp",EDGE,"E15.2.1"),sQuery(id+"F0.wireOp",EDGE,"E15.2.2"),sQuery(id+"F0.wireOp",EDGE,"E15.2.5"),sQuery(id+"F0.wireOp",EDGE,"E15.2.6"),sQuery(id+"F0.wireOp",EDGE,"E15.2.7"),sQuery(id+"F0.wireOp",EDGE,"E15.2.8")])],"isStart":true})],"blendedInto":[makeQuery(id+"F1.opExtrude","CAP_FACE",FACE,{"disambiguationData":[OSD([sQuery(id+"F0.wireOp",EDGE,"E1"),sQuery(id+"F0.wireOp",EDGE,"E2"),sQuery(id+"F0.wireOp",EDGE,"E3"),sQuery(id+"F0.wireOp",EDGE,"E13.0"),sQuery(id+"F0.wireOp",EDGE,"E13.1"),sQuery(id+"F0.wireOp",EDGE,"E14.0"),subQ1,sQuery(id+"F0.wireOp",EDGE,"E15.1.1"),sQuery(id+"F0.wireOp",EDGE,"E15.1.2"),sQuery(id+"F0.wireOp",EDGE,"E15.1.5"),sQuery(id+"F0.wireOp",EDGE,"E15.1.6"),sQuery(id+"F0.wireOp",EDGE,"E15.1.7"),subQ0,sQuery(id+"F0.wireOp",EDGE,"E15.2.1"),sQuery(id+"F0.wireOp",EDGE,"E15.2.2"),sQuery(id+"F0.wireOp",EDGE,"E15.2.5"),sQuery(id+"F0.wireOp",EDGE,"E15.2.6"),sQuery(id+"F0.wireOp",EDGE,"E15.2.7"),sQuery(id+"F0.wireOp",EDGE,"E15.2.8")])],"isStart":true})]});}
            var Q12;
            {var subQ0=sQuery(id+"F0.wireOp",EDGE,"E14.0");var subQ1=sQuery(id+"F0.wireOp",EDGE,"E1");Q12=makeQuery(id+"F2.opFillet","BLEND_EDGE",EDGE,{"blendedFrom":[makeQuery(id+"F1.opExtrude","SWEPT_EDGE",EDGE,{"disambiguationData":[OSD([subQ1,subQ0])]}),makeQuery(id+"F1.opExtrude","CAP_FACE",FACE,{"disambiguationData":[OSD([subQ1,sQuery(id+"F0.wireOp",EDGE,"E2"),sQuery(id+"F0.wireOp",EDGE,"E3"),sQuery(id+"F0.wireOp",EDGE,"E13.0"),sQuery(id+"F0.wireOp",EDGE,"E13.1"),subQ0,sQuery(id+"F0.wireOp",EDGE,"E14.1"),sQuery(id+"F0.wireOp",EDGE,"E15.1.1"),sQuery(id+"F0.wireOp",EDGE,"E15.1.2"),sQuery(id+"F0.wireOp",EDGE,"E15.1.5"),sQuery(id+"F0.wireOp",EDGE,"E15.1.6"),sQuery(id+"F0.wireOp",EDGE,"E15.1.7"),sQuery(id+"F0.wireOp",EDGE,"E15.1.8"),sQuery(id+"F0.wireOp",EDGE,"E15.2.1"),sQuery(id+"F0.wireOp",EDGE,"E15.2.2"),sQuery(id+"F0.wireOp",EDGE,"E15.2.5"),sQuery(id+"F0.wireOp",EDGE,"E15.2.6"),sQuery(id+"F0.wireOp",EDGE,"E15.2.7"),sQuery(id+"F0.wireOp",EDGE,"E15.2.8")])],"isStart":true})],"blendedInto":[makeQuery(id+"F1.opExtrude","CAP_FACE",FACE,{"disambiguationData":[OSD([subQ1,sQuery(id+"F0.wireOp",EDGE,"E2"),sQuery(id+"F0.wireOp",EDGE,"E3"),sQuery(id+"F0.wireOp",EDGE,"E13.0"),sQuery(id+"F0.wireOp",EDGE,"E13.1"),subQ0,sQuery(id+"F0.wireOp",EDGE,"E14.1"),sQuery(id+"F0.wireOp",EDGE,"E15.1.1"),sQuery(id+"F0.wireOp",EDGE,"E15.1.2"),sQuery(id+"F0.wireOp",EDGE,"E15.1.5"),sQuery(id+"F0.wireOp",EDGE,"E15.1.6"),sQuery(id+"F0.wireOp",EDGE,"E15.1.7"),sQuery(id+"F0.wireOp",EDGE,"E15.1.8"),sQuery(id+"F0.wireOp",EDGE,"E15.2.1"),sQuery(id+"F0.wireOp",EDGE,"E15.2.2"),sQuery(id+"F0.wireOp",EDGE,"E15.2.5"),sQuery(id+"F0.wireOp",EDGE,"E15.2.6"),sQuery(id+"F0.wireOp",EDGE,"E15.2.7"),sQuery(id+"F0.wireOp",EDGE,"E15.2.8")])],"isStart":true})]});}
            var Q13;
            Q13=makeQuery(id+"F1.opExtrude","CAP_EDGE",EDGE,{"disambiguationData":[OSD([sQuery(id+"F0.wireOp",EDGE,"E1")])],"isStart":true});
            var Q14;
            {var subQ0=sQuery(id+"F0.wireOp",EDGE,"E13.0");var subQ1=sQuery(id+"F0.wireOp",EDGE,"E1");Q14=makeQuery(id+"F2.opFillet","BLEND_EDGE",EDGE,{"blendedFrom":[makeQuery(id+"F1.opExtrude","SWEPT_EDGE",EDGE,{"disambiguationData":[OSD([subQ1,subQ0])]}),makeQuery(id+"F1.opExtrude","CAP_FACE",FACE,{"disambiguationData":[OSD([subQ1,sQuery(id+"F0.wireOp",EDGE,"E2"),sQuery(id+"F0.wireOp",EDGE,"E3"),subQ0,sQuery(id+"F0.wireOp",EDGE,"E13.1"),sQuery(id+"F0.wireOp",EDGE,"E14.0"),sQuery(id+"F0.wireOp",EDGE,"E14.1"),sQuery(id+"F0.wireOp",EDGE,"E15.1.1"),sQuery(id+"F0.wireOp",EDGE,"E15.1.2"),sQuery(id+"F0.wireOp",EDGE,"E15.1.5"),sQuery(id+"F0.wireOp",EDGE,"E15.1.6"),sQuery(id+"F0.wireOp",EDGE,"E15.1.7"),sQuery(id+"F0.wireOp",EDGE,"E15.1.8"),sQuery(id+"F0.wireOp",EDGE,"E15.2.1"),sQuery(id+"F0.wireOp",EDGE,"E15.2.2"),sQuery(id+"F0.wireOp",EDGE,"E15.2.5"),sQuery(id+"F0.wireOp",EDGE,"E15.2.6"),sQuery(id+"F0.wireOp",EDGE,"E15.2.7"),sQuery(id+"F0.wireOp",EDGE,"E15.2.8")])],"isStart":true})],"blendedInto":[makeQuery(id+"F1.opExtrude","CAP_FACE",FACE,{"disambiguationData":[OSD([subQ1,sQuery(id+"F0.wireOp",EDGE,"E2"),sQuery(id+"F0.wireOp",EDGE,"E3"),subQ0,sQuery(id+"F0.wireOp",EDGE,"E13.1"),sQuery(id+"F0.wireOp",EDGE,"E14.0"),sQuery(id+"F0.wireOp",EDGE,"E14.1"),sQuery(id+"F0.wireOp",EDGE,"E15.1.1"),sQuery(id+"F0.wireOp",EDGE,"E15.1.2"),sQuery(id+"F0.wireOp",EDGE,"E15.1.5"),sQuery(id+"F0.wireOp",EDGE,"E15.1.6"),sQuery(id+"F0.wireOp",EDGE,"E15.1.7"),sQuery(id+"F0.wireOp",EDGE,"E15.1.8"),sQuery(id+"F0.wireOp",EDGE,"E15.2.1"),sQuery(id+"F0.wireOp",EDGE,"E15.2.2"),sQuery(id+"F0.wireOp",EDGE,"E15.2.5"),sQuery(id+"F0.wireOp",EDGE,"E15.2.6"),sQuery(id+"F0.wireOp",EDGE,"E15.2.7"),sQuery(id+"F0.wireOp",EDGE,"E15.2.8")])],"isStart":true})]});}
            var Q15;
            {var subQ0=sQuery(id+"F0.wireOp",EDGE,"E15.2.7");var subQ1=sQuery(id+"F0.wireOp",EDGE,"E13.1");Q15=makeQuery(id+"F3.opFillet","BLEND_EDGE",EDGE,{"blendedFrom":[makeQuery(id+"F1.opExtrude","SWEPT_EDGE",EDGE,{"disambiguationData":[OSD([subQ1,subQ0])]}),makeQuery(id+"F1.opExtrude","CAP_FACE",FACE,{"disambiguationData":[OSD([sQuery(id+"F0.wireOp",EDGE,"E1"),sQuery(id+"F0.wireOp",EDGE,"E2"),sQuery(id+"F0.wireOp",EDGE,"E3"),sQuery(id+"F0.wireOp",EDGE,"E13.0"),subQ1,sQuery(id+"F0.wireOp",EDGE,"E14.0"),sQuery(id+"F0.wireOp",EDGE,"E14.1"),sQuery(id+"F0.wireOp",EDGE,"E15.1.1"),sQuery(id+"F0.wireOp",EDGE,"E15.1.2"),sQuery(id+"F0.wireOp",EDGE,"E15.1.5"),sQuery(id+"F0.wireOp",EDGE,"E15.1.6"),sQuery(id+"F0.wireOp",EDGE,"E15.1.7"),sQuery(id+"F0.wireOp",EDGE,"E15.1.8"),sQuery(id+"F0.wireOp",EDGE,"E15.2.1"),sQuery(id+"F0.wireOp",EDGE,"E15.2.2"),sQuery(id+"F0.wireOp",EDGE,"E15.2.5"),sQuery(id+"F0.wireOp",EDGE,"E15.2.6"),subQ0,sQuery(id+"F0.wireOp",EDGE,"E15.2.8")])],"isStart":true})],"blendedInto":[makeQuery(id+"F1.opExtrude","CAP_FACE",FACE,{"disambiguationData":[OSD([sQuery(id+"F0.wireOp",EDGE,"E1"),sQuery(id+"F0.wireOp",EDGE,"E2"),sQuery(id+"F0.wireOp",EDGE,"E3"),sQuery(id+"F0.wireOp",EDGE,"E13.0"),subQ1,sQuery(id+"F0.wireOp",EDGE,"E14.0"),sQuery(id+"F0.wireOp",EDGE,"E14.1"),sQuery(id+"F0.wireOp",EDGE,"E15.1.1"),sQuery(id+"F0.wireOp",EDGE,"E15.1.2"),sQuery(id+"F0.wireOp",EDGE,"E15.1.5"),sQuery(id+"F0.wireOp",EDGE,"E15.1.6"),sQuery(id+"F0.wireOp",EDGE,"E15.1.7"),sQuery(id+"F0.wireOp",EDGE,"E15.1.8"),sQuery(id+"F0.wireOp",EDGE,"E15.2.1"),sQuery(id+"F0.wireOp",EDGE,"E15.2.2"),sQuery(id+"F0.wireOp",EDGE,"E15.2.5"),sQuery(id+"F0.wireOp",EDGE,"E15.2.6"),subQ0,sQuery(id+"F0.wireOp",EDGE,"E15.2.8")])],"isStart":true})]});}
            var Q16;
            Q16=makeQuery(id+"F1.opExtrude","CAP_EDGE",EDGE,{"disambiguationData":[OSD([sQuery(id+"F0.wireOp",EDGE,"E15.2.6")])],"isStart":true});
            var Q17;
            {var subQ0=sQuery(id+"F0.wireOp",EDGE,"E15.2.6");var subQ1=sQuery(id+"F0.wireOp",EDGE,"E15.2.1");Q17=makeQuery(id+"F2.opFillet","BLEND_EDGE",EDGE,{"blendedFrom":[makeQuery(id+"F1.opExtrude","SWEPT_EDGE",EDGE,{"disambiguationData":[OSD([subQ1,subQ0])]}),makeQuery(id+"F1.opExtrude","CAP_FACE",FACE,{"disambiguationData":[OSD([sQuery(id+"F0.wireOp",EDGE,"E1"),sQuery(id+"F0.wireOp",EDGE,"E2"),sQuery(id+"F0.wireOp",EDGE,"E3"),sQuery(id+"F0.wireOp",EDGE,"E13.0"),sQuery(id+"F0.wireOp",EDGE,"E13.1"),sQuery(id+"F0.wireOp",EDGE,"E14.0"),sQuery(id+"F0.wireOp",EDGE,"E14.1"),sQuery(id+"F0.wireOp",EDGE,"E15.1.1"),sQuery(id+"F0.wireOp",EDGE,"E15.1.2"),sQuery(id+"F0.wireOp",EDGE,"E15.1.5"),sQuery(id+"F0.wireOp",EDGE,"E15.1.6"),sQuery(id+"F0.wireOp",EDGE,"E15.1.7"),sQuery(id+"F0.wireOp",EDGE,"E15.1.8"),subQ1,sQuery(id+"F0.wireOp",EDGE,"E15.2.2"),sQuery(id+"F0.wireOp",EDGE,"E15.2.5"),subQ0,sQuery(id+"F0.wireOp",EDGE,"E15.2.7"),sQuery(id+"F0.wireOp",EDGE,"E15.2.8")])],"isStart":true})],"blendedInto":[makeQuery(id+"F1.opExtrude","CAP_FACE",FACE,{"disambiguationData":[OSD([sQuery(id+"F0.wireOp",EDGE,"E1"),sQuery(id+"F0.wireOp",EDGE,"E2"),sQuery(id+"F0.wireOp",EDGE,"E3"),sQuery(id+"F0.wireOp",EDGE,"E13.0"),sQuery(id+"F0.wireOp",EDGE,"E13.1"),sQuery(id+"F0.wireOp",EDGE,"E14.0"),sQuery(id+"F0.wireOp",EDGE,"E14.1"),sQuery(id+"F0.wireOp",EDGE,"E15.1.1"),sQuery(id+"F0.wireOp",EDGE,"E15.1.2"),sQuery(id+"F0.wireOp",EDGE,"E15.1.5"),sQuery(id+"F0.wireOp",EDGE,"E15.1.6"),sQuery(id+"F0.wireOp",EDGE,"E15.1.7"),sQuery(id+"F0.wireOp",EDGE,"E15.1.8"),subQ1,sQuery(id+"F0.wireOp",EDGE,"E15.2.2"),sQuery(id+"F0.wireOp",EDGE,"E15.2.5"),subQ0,sQuery(id+"F0.wireOp",EDGE,"E15.2.7"),sQuery(id+"F0.wireOp",EDGE,"E15.2.8")])],"isStart":true})]});}
            var Q18;
            {var subQ0=sQuery(id+"F0.wireOp",EDGE,"E15.2.6");var subQ1=sQuery(id+"F0.wireOp",EDGE,"E15.2.2");Q18=makeQuery(id+"F2.opFillet","BLEND_EDGE",EDGE,{"blendedFrom":[makeQuery(id+"F1.opExtrude","SWEPT_EDGE",EDGE,{"disambiguationData":[OSD([subQ1,subQ0])]}),makeQuery(id+"F1.opExtrude","CAP_FACE",FACE,{"disambiguationData":[OSD([sQuery(id+"F0.wireOp",EDGE,"E1"),sQuery(id+"F0.wireOp",EDGE,"E2"),sQuery(id+"F0.wireOp",EDGE,"E3"),sQuery(id+"F0.wireOp",EDGE,"E13.0"),sQuery(id+"F0.wireOp",EDGE,"E13.1"),sQuery(id+"F0.wireOp",EDGE,"E14.0"),sQuery(id+"F0.wireOp",EDGE,"E14.1"),sQuery(id+"F0.wireOp",EDGE,"E15.1.1"),sQuery(id+"F0.wireOp",EDGE,"E15.1.2"),sQuery(id+"F0.wireOp",EDGE,"E15.1.5"),sQuery(id+"F0.wireOp",EDGE,"E15.1.6"),sQuery(id+"F0.wireOp",EDGE,"E15.1.7"),sQuery(id+"F0.wireOp",EDGE,"E15.1.8"),sQuery(id+"F0.wireOp",EDGE,"E15.2.1"),subQ1,sQuery(id+"F0.wireOp",EDGE,"E15.2.5"),subQ0,sQuery(id+"F0.wireOp",EDGE,"E15.2.7"),sQuery(id+"F0.wireOp",EDGE,"E15.2.8")])],"isStart":true})],"blendedInto":[makeQuery(id+"F1.opExtrude","CAP_FACE",FACE,{"disambiguationData":[OSD([sQuery(id+"F0.wireOp",EDGE,"E1"),sQuery(id+"F0.wireOp",EDGE,"E2"),sQuery(id+"F0.wireOp",EDGE,"E3"),sQuery(id+"F0.wireOp",EDGE,"E13.0"),sQuery(id+"F0.wireOp",EDGE,"E13.1"),sQuery(id+"F0.wireOp",EDGE,"E14.0"),sQuery(id+"F0.wireOp",EDGE,"E14.1"),sQuery(id+"F0.wireOp",EDGE,"E15.1.1"),sQuery(id+"F0.wireOp",EDGE,"E15.1.2"),sQuery(id+"F0.wireOp",EDGE,"E15.1.5"),sQuery(id+"F0.wireOp",EDGE,"E15.1.6"),sQuery(id+"F0.wireOp",EDGE,"E15.1.7"),sQuery(id+"F0.wireOp",EDGE,"E15.1.8"),sQuery(id+"F0.wireOp",EDGE,"E15.2.1"),subQ1,sQuery(id+"F0.wireOp",EDGE,"E15.2.5"),subQ0,sQuery(id+"F0.wireOp",EDGE,"E15.2.7"),sQuery(id+"F0.wireOp",EDGE,"E15.2.8")])],"isStart":true})]});}
            var Q19;
            {var subQ0=sQuery(id+"F0.wireOp",EDGE,"E15.2.8");var subQ1=sQuery(id+"F0.wireOp",EDGE,"E15.1.7");Q19=makeQuery(id+"F3.opFillet","BLEND_EDGE",EDGE,{"blendedFrom":[makeQuery(id+"F1.opExtrude","SWEPT_EDGE",EDGE,{"disambiguationData":[OSD([sQuery(id+"F0.wireOp",EDGE,"E6"),subQ1,subQ0])]}),makeQuery(id+"F1.opExtrude","CAP_FACE",FACE,{"disambiguationData":[OSD([sQuery(id+"F0.wireOp",EDGE,"E1"),sQuery(id+"F0.wireOp",EDGE,"E2"),sQuery(id+"F0.wireOp",EDGE,"E3"),sQuery(id+"F0.wireOp",EDGE,"E13.0"),sQuery(id+"F0.wireOp",EDGE,"E13.1"),sQuery(id+"F0.wireOp",EDGE,"E14.0"),sQuery(id+"F0.wireOp",EDGE,"E14.1"),sQuery(id+"F0.wireOp",EDGE,"E15.1.1"),sQuery(id+"F0.wireOp",EDGE,"E15.1.2"),sQuery(id+"F0.wireOp",EDGE,"E15.1.5"),sQuery(id+"F0.wireOp",EDGE,"E15.1.6"),subQ1,sQuery(id+"F0.wireOp",EDGE,"E15.1.8"),sQuery(id+"F0.wireOp",EDGE,"E15.2.1"),sQuery(id+"F0.wireOp",EDGE,"E15.2.2"),sQuery(id+"F0.wireOp",EDGE,"E15.2.5"),sQuery(id+"F0.wireOp",EDGE,"E15.2.6"),sQuery(id+"F0.wireOp",EDGE,"E15.2.7"),subQ0])],"isStart":true})],"blendedInto":[makeQuery(id+"F1.opExtrude","CAP_FACE",FACE,{"disambiguationData":[OSD([sQuery(id+"F0.wireOp",EDGE,"E1"),sQuery(id+"F0.wireOp",EDGE,"E2"),sQuery(id+"F0.wireOp",EDGE,"E3"),sQuery(id+"F0.wireOp",EDGE,"E13.0"),sQuery(id+"F0.wireOp",EDGE,"E13.1"),sQuery(id+"F0.wireOp",EDGE,"E14.0"),sQuery(id+"F0.wireOp",EDGE,"E14.1"),sQuery(id+"F0.wireOp",EDGE,"E15.1.1"),sQuery(id+"F0.wireOp",EDGE,"E15.1.2"),sQuery(id+"F0.wireOp",EDGE,"E15.1.5"),sQuery(id+"F0.wireOp",EDGE,"E15.1.6"),subQ1,sQuery(id+"F0.wireOp",EDGE,"E15.1.8"),sQuery(id+"F0.wireOp",EDGE,"E15.2.1"),sQuery(id+"F0.wireOp",EDGE,"E15.2.2"),sQuery(id+"F0.wireOp",EDGE,"E15.2.5"),sQuery(id+"F0.wireOp",EDGE,"E15.2.6"),sQuery(id+"F0.wireOp",EDGE,"E15.2.7"),subQ0])],"isStart":true})]});}
            var Q20;
            Q20=makeQuery(id+"F1.opExtrude","CAP_EDGE",EDGE,{"disambiguationData":[OSD([sQuery(id+"F0.wireOp",EDGE,"E15.1.6")])],"isStart":true});
            var Q21;
            {var subQ0=sQuery(id+"F0.wireOp",EDGE,"E15.1.6");var subQ1=sQuery(id+"F0.wireOp",EDGE,"E15.1.1");Q21=makeQuery(id+"F2.opFillet","BLEND_EDGE",EDGE,{"blendedFrom":[makeQuery(id+"F1.opExtrude","SWEPT_EDGE",EDGE,{"disambiguationData":[OSD([subQ1,subQ0])]}),makeQuery(id+"F1.opExtrude","CAP_FACE",FACE,{"disambiguationData":[OSD([sQuery(id+"F0.wireOp",EDGE,"E1"),sQuery(id+"F0.wireOp",EDGE,"E2"),sQuery(id+"F0.wireOp",EDGE,"E3"),sQuery(id+"F0.wireOp",EDGE,"E13.0"),sQuery(id+"F0.wireOp",EDGE,"E13.1"),sQuery(id+"F0.wireOp",EDGE,"E14.0"),sQuery(id+"F0.wireOp",EDGE,"E14.1"),subQ1,sQuery(id+"F0.wireOp",EDGE,"E15.1.2"),sQuery(id+"F0.wireOp",EDGE,"E15.1.5"),subQ0,sQuery(id+"F0.wireOp",EDGE,"E15.1.7"),sQuery(id+"F0.wireOp",EDGE,"E15.1.8"),sQuery(id+"F0.wireOp",EDGE,"E15.2.1"),sQuery(id+"F0.wireOp",EDGE,"E15.2.2"),sQuery(id+"F0.wireOp",EDGE,"E15.2.5"),sQuery(id+"F0.wireOp",EDGE,"E15.2.6"),sQuery(id+"F0.wireOp",EDGE,"E15.2.7"),sQuery(id+"F0.wireOp",EDGE,"E15.2.8")])],"isStart":true})],"blendedInto":[makeQuery(id+"F1.opExtrude","CAP_FACE",FACE,{"disambiguationData":[OSD([sQuery(id+"F0.wireOp",EDGE,"E1"),sQuery(id+"F0.wireOp",EDGE,"E2"),sQuery(id+"F0.wireOp",EDGE,"E3"),sQuery(id+"F0.wireOp",EDGE,"E13.0"),sQuery(id+"F0.wireOp",EDGE,"E13.1"),sQuery(id+"F0.wireOp",EDGE,"E14.0"),sQuery(id+"F0.wireOp",EDGE,"E14.1"),subQ1,sQuery(id+"F0.wireOp",EDGE,"E15.1.2"),sQuery(id+"F0.wireOp",EDGE,"E15.1.5"),subQ0,sQuery(id+"F0.wireOp",EDGE,"E15.1.7"),sQuery(id+"F0.wireOp",EDGE,"E15.1.8"),sQuery(id+"F0.wireOp",EDGE,"E15.2.1"),sQuery(id+"F0.wireOp",EDGE,"E15.2.2"),sQuery(id+"F0.wireOp",EDGE,"E15.2.5"),sQuery(id+"F0.wireOp",EDGE,"E15.2.6"),sQuery(id+"F0.wireOp",EDGE,"E15.2.7"),sQuery(id+"F0.wireOp",EDGE,"E15.2.8")])],"isStart":true})]});}
            var Q22;
            {var subQ0=sQuery(id+"F0.wireOp",EDGE,"E15.1.6");var subQ1=sQuery(id+"F0.wireOp",EDGE,"E15.1.2");Q22=makeQuery(id+"F2.opFillet","BLEND_EDGE",EDGE,{"blendedFrom":[makeQuery(id+"F1.opExtrude","SWEPT_EDGE",EDGE,{"disambiguationData":[OSD([subQ1,subQ0])]}),makeQuery(id+"F1.opExtrude","CAP_FACE",FACE,{"disambiguationData":[OSD([sQuery(id+"F0.wireOp",EDGE,"E1"),sQuery(id+"F0.wireOp",EDGE,"E2"),sQuery(id+"F0.wireOp",EDGE,"E3"),sQuery(id+"F0.wireOp",EDGE,"E13.0"),sQuery(id+"F0.wireOp",EDGE,"E13.1"),sQuery(id+"F0.wireOp",EDGE,"E14.0"),sQuery(id+"F0.wireOp",EDGE,"E14.1"),sQuery(id+"F0.wireOp",EDGE,"E15.1.1"),subQ1,sQuery(id+"F0.wireOp",EDGE,"E15.1.5"),subQ0,sQuery(id+"F0.wireOp",EDGE,"E15.1.7"),sQuery(id+"F0.wireOp",EDGE,"E15.1.8"),sQuery(id+"F0.wireOp",EDGE,"E15.2.1"),sQuery(id+"F0.wireOp",EDGE,"E15.2.2"),sQuery(id+"F0.wireOp",EDGE,"E15.2.5"),sQuery(id+"F0.wireOp",EDGE,"E15.2.6"),sQuery(id+"F0.wireOp",EDGE,"E15.2.7"),sQuery(id+"F0.wireOp",EDGE,"E15.2.8")])],"isStart":true})],"blendedInto":[makeQuery(id+"F1.opExtrude","CAP_FACE",FACE,{"disambiguationData":[OSD([sQuery(id+"F0.wireOp",EDGE,"E1"),sQuery(id+"F0.wireOp",EDGE,"E2"),sQuery(id+"F0.wireOp",EDGE,"E3"),sQuery(id+"F0.wireOp",EDGE,"E13.0"),sQuery(id+"F0.wireOp",EDGE,"E13.1"),sQuery(id+"F0.wireOp",EDGE,"E14.0"),sQuery(id+"F0.wireOp",EDGE,"E14.1"),sQuery(id+"F0.wireOp",EDGE,"E15.1.1"),subQ1,sQuery(id+"F0.wireOp",EDGE,"E15.1.5"),subQ0,sQuery(id+"F0.wireOp",EDGE,"E15.1.7"),sQuery(id+"F0.wireOp",EDGE,"E15.1.8"),sQuery(id+"F0.wireOp",EDGE,"E15.2.1"),sQuery(id+"F0.wireOp",EDGE,"E15.2.2"),sQuery(id+"F0.wireOp",EDGE,"E15.2.5"),sQuery(id+"F0.wireOp",EDGE,"E15.2.6"),sQuery(id+"F0.wireOp",EDGE,"E15.2.7"),sQuery(id+"F0.wireOp",EDGE,"E15.2.8")])],"isStart":true})]});}
            fillet(context, id + "F5", {"entities" : qUnion([Q0, Q1, Q2, Q3, Q4, Q5, Q6, Q7, Q8, Q9, Q10, Q11, Q12, Q13, Q14, Q15, Q16, Q17, Q18, Q19, Q20, Q21, Q22]), "radius" : 2.54 * mm, "tangentPropagation" : true, "allowEdgeOverflow" : false});
        }
    });
